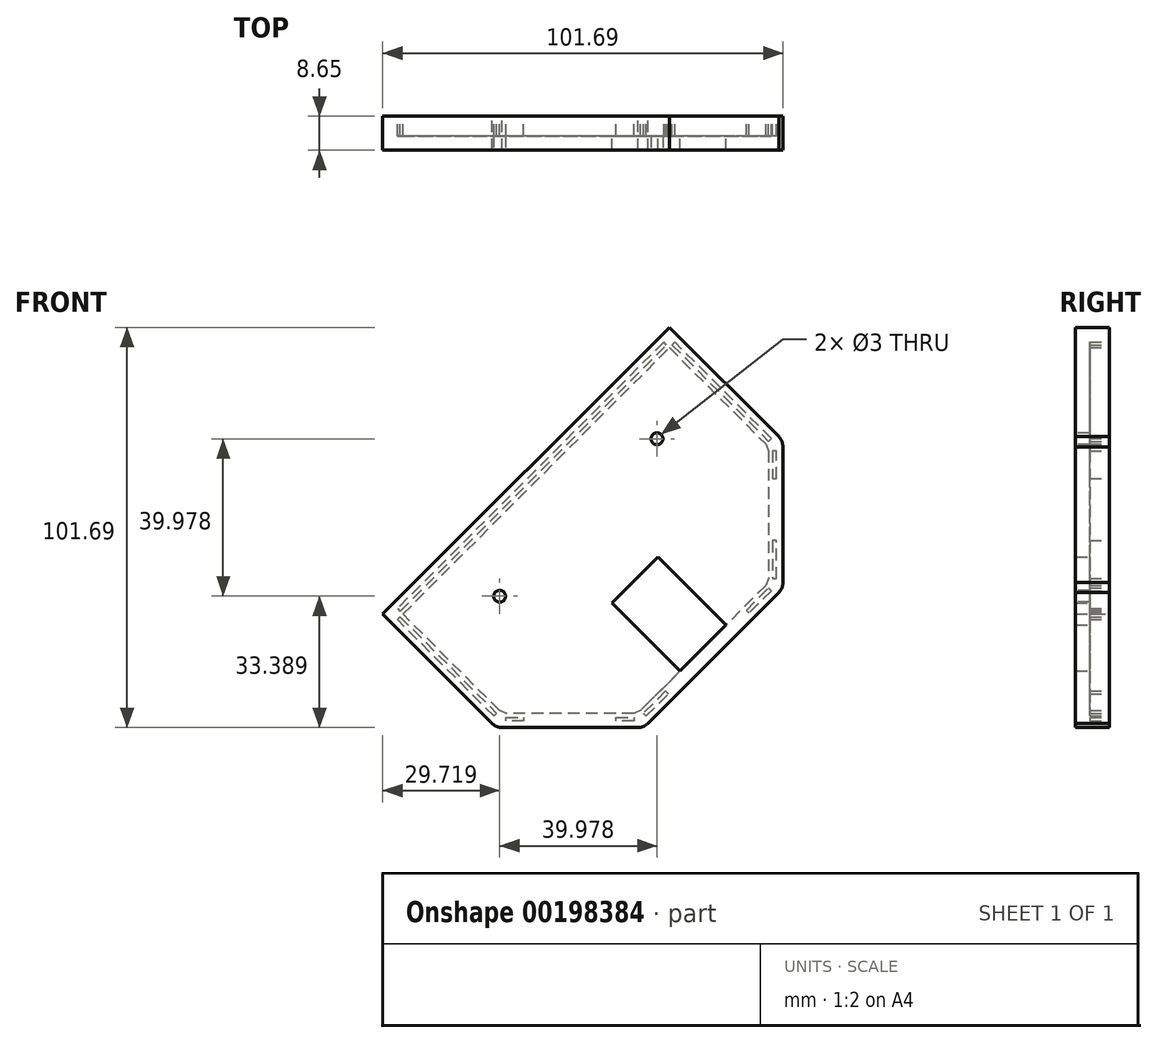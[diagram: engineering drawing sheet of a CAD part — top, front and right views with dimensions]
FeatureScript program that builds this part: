
annotation { "Feature Type Name" : "Feature", "Feature Type Description" : "" }
export const myFeature = defineFeature(function(context is Context, id is Id, definition is map)
    precondition{}
    {
        {
            var Q0;
            Q0=qCreatedBy(makeId("Front.planeOp"),FACE);
            var sketch = newSketch(context, id + "F0", { "sketchPlane" : qUnion([Q0])});
            skLineSegment(sketch, "E0", {"start": v(6.59, 67.44) * mm, "end": v(-66.27, -5.41) * mm});
            skLineSegment(sketch, "E1", {"start": v(-66.27, -5.41) * mm, "end": v(-38.5, -33.18) * mm});
            skFitSpline(sketch, "E2", {"points": [v(-38.5, -33.18) * mm, v(-37.32, -33.98) * mm, v(-35.92, -34.25) * mm], "startDerivative": vector(2.26, -1.84) * mm, "endDerivative": vector(2.9, -0.3) * mm});
            skLineSegment(sketch, "E3", {"start": v(-35.92, -34.25) * mm, "end": v(-1.44, -34.25) * mm});
            skFitSpline(sketch, "E4", {"points": [v(-1.44, -34.25) * mm, v(-0.05, -33.98) * mm, v(1.14, -33.18) * mm], "startDerivative": vector(2.9, 0.3) * mm, "endDerivative": vector(2.26, 1.84) * mm});
            skLineSegment(sketch, "E5", {"start": v(1.14, -33.18) * mm, "end": v(34.35, 0.03) * mm});
            skFitSpline(sketch, "E6", {"points": [v(35.42, 37.1) * mm, v(35.15, 38.49) * mm, v(34.35, 39.67) * mm], "startDerivative": vector(-0.3, 2.9) * mm, "endDerivative": vector(-1.84, 2.26) * mm});
            skLineSegment(sketch, "E7", {"start": v(34.35, 39.67) * mm, "end": v(6.59, 67.44) * mm});
            skLineSegment(sketch, "E8", {"start": v(6.59, 62.28) * mm, "end": v(31.07, 37.8) * mm});
            skLineSegment(sketch, "E9", {"start": v(31.07, 37.8) * mm, "end": v(31.77, 36.1) * mm});
            skLineSegment(sketch, "E10", {"start": v(31.77, 36.1) * mm, "end": v(31.77, 3.61) * mm});
            skLineSegment(sketch, "E11", {"start": v(31.77, 3.61) * mm, "end": v(31.07, 1.9) * mm});
            skLineSegment(sketch, "E12", {"start": v(31.07, 1.9) * mm, "end": v(25.42, -3.74) * mm});
            skLineSegment(sketch, "E13", {"start": v(25.42, -3.74) * mm, "end": v(-0.74, -29.9) * mm});
            skLineSegment(sketch, "E14", {"start": v(-0.74, -29.9) * mm, "end": v(-2.44, -30.6) * mm});
            skLineSegment(sketch, "E15", {"start": v(-2.44, -30.6) * mm, "end": v(-6.93, -30.6) * mm});
            skLineSegment(sketch, "E16", {"start": v(-6.93, -30.6) * mm, "end": v(-30.43, -30.6) * mm});
            skLineSegment(sketch, "E17", {"start": v(-30.43, -30.6) * mm, "end": v(-34.92, -30.6) * mm});
            skLineSegment(sketch, "E18", {"start": v(-34.92, -30.6) * mm, "end": v(-36.63, -29.9) * mm});
            skLineSegment(sketch, "E19", {"start": v(-36.63, -29.9) * mm, "end": v(-61.1, -5.41) * mm});
            skLineSegment(sketch, "E20", {"start": v(-61.1, -5.41) * mm, "end": v(6.59, 62.28) * mm});
            skLineSegment(sketch, "E21", {"start": v(32.48, 39.21) * mm, "end": v(8, 63.7) * mm});
            skLineSegment(sketch, "E22", {"start": v(8, 63.7) * mm, "end": v(7.3, 62.99) * mm});
            skLineSegment(sketch, "E23", {"start": v(7.3, 62.99) * mm, "end": v(31.77, 38.5) * mm});
            skLineSegment(sketch, "E24", {"start": v(31.77, 38.5) * mm, "end": v(32.48, 39.21) * mm});
            skLineSegment(sketch, "E25", {"start": v(5.17, 63.7) * mm, "end": v(-62.52, -4) * mm});
            skLineSegment(sketch, "E26", {"start": v(-62.52, -4) * mm, "end": v(-61.81, -4.7) * mm});
            skLineSegment(sketch, "E27", {"start": v(-61.81, -4.7) * mm, "end": v(5.88, 62.99) * mm});
            skLineSegment(sketch, "E28", {"start": v(5.88, 62.99) * mm, "end": v(5.17, 63.7) * mm});
            skLineSegment(sketch, "E29", {"start": v(33.77, 36.1) * mm, "end": v(32.77, 36.1) * mm});
            skLineSegment(sketch, "E30", {"start": v(32.77, 36.1) * mm, "end": v(32.77, 28.98) * mm});
            skLineSegment(sketch, "E31", {"start": v(32.77, 28.98) * mm, "end": v(33.77, 28.98) * mm});
            skLineSegment(sketch, "E32", {"start": v(33.77, 28.98) * mm, "end": v(33.77, 36.1) * mm});
            skLineSegment(sketch, "E33", {"start": v(-37.33, -30.6) * mm, "end": v(-38.04, -31.31) * mm});
            skLineSegment(sketch, "E34", {"start": v(-38.04, -31.31) * mm, "end": v(-62.52, -6.83) * mm});
            skLineSegment(sketch, "E35", {"start": v(-62.52, -6.83) * mm, "end": v(-61.81, -6.12) * mm});
            skLineSegment(sketch, "E36", {"start": v(-61.81, -6.12) * mm, "end": v(-37.33, -30.6) * mm});
            skLineSegment(sketch, "E37", {"start": v(-30.43, -32.6) * mm, "end": v(-34.92, -32.6) * mm});
            skLineSegment(sketch, "E38", {"start": v(-34.92, -32.6) * mm, "end": v(-34.92, -31.6) * mm});
            skLineSegment(sketch, "E39", {"start": v(-34.92, -31.6) * mm, "end": v(-30.43, -31.6) * mm});
            skLineSegment(sketch, "E40", {"start": v(-30.43, -31.6) * mm, "end": v(-30.43, -32.6) * mm});
            skLineSegment(sketch, "E41", {"start": v(-2.44, -32.6) * mm, "end": v(-6.93, -32.6) * mm});
            skLineSegment(sketch, "E42", {"start": v(-6.93, -32.6) * mm, "end": v(-6.93, -31.6) * mm});
            skLineSegment(sketch, "E43", {"start": v(-6.93, -31.6) * mm, "end": v(-2.44, -31.6) * mm});
            skLineSegment(sketch, "E44", {"start": v(-2.44, -31.6) * mm, "end": v(-2.44, -32.6) * mm});
            skLineSegment(sketch, "E45", {"start": v(6.33, -25.66) * mm, "end": v(5.62, -24.95) * mm});
            skLineSegment(sketch, "E46", {"start": v(5.62, -24.95) * mm, "end": v(-0.03, -30.6) * mm});
            skLineSegment(sketch, "E47", {"start": v(-0.03, -30.6) * mm, "end": v(0.68, -31.31) * mm});
            skLineSegment(sketch, "E48", {"start": v(0.68, -31.31) * mm, "end": v(6.33, -25.66) * mm});
            skLineSegment(sketch, "E49", {"start": v(26.83, -5.16) * mm, "end": v(26.13, -4.45) * mm});
            skLineSegment(sketch, "E50", {"start": v(26.13, -4.45) * mm, "end": v(31.77, 1.2) * mm});
            skLineSegment(sketch, "E51", {"start": v(31.77, 1.2) * mm, "end": v(32.48, 0.5) * mm});
            skLineSegment(sketch, "E52", {"start": v(32.48, 0.5) * mm, "end": v(26.83, -5.16) * mm});
            skLineSegment(sketch, "E53", {"start": v(33.77, 3.61) * mm, "end": v(33.77, 13.23) * mm});
            skLineSegment(sketch, "E54", {"start": v(33.77, 13.23) * mm, "end": v(32.77, 13.23) * mm});
            skLineSegment(sketch, "E55", {"start": v(32.77, 13.23) * mm, "end": v(32.77, 3.61) * mm});
            skLineSegment(sketch, "E56", {"start": v(32.77, 3.61) * mm, "end": v(33.77, 3.61) * mm});
            skLineSegment(sketch, "E57", {"start": v(17.75, -16.58) * mm, "end": v(-0.03, 1.2) * mm});
            skFitSpline(sketch, "E58", {"points": [v(34.35, 0.03) * mm, v(35.15, 1.22) * mm, v(35.42, 2.61) * mm], "startDerivative": vector(1.84, 2.26) * mm, "endDerivative": vector(0.3, 2.9) * mm});
            skLineSegment(sketch, "E59", {"start": v(35.42, 37.1) * mm, "end": v(35.42, 2.61) * mm});
            skSolve(sketch);
        }
        {
            var Q0;
            Q0=makeQuery(id+"F0.imprint","IMPRINT",FACE,{"disambiguationData":[TD([[makeQuery(id+"F0.imprint","IMPRINT",EDGE,{"derivedFrom":sQuery(id+"F0.wireOp",EDGE,"E29")}),1.0]])]});
            var Q1;
            Q1=makeQuery(id+"F0.imprint","IMPRINT",FACE,{"disambiguationData":[TD([[makeQuery(id+"F0.imprint","IMPRINT",EDGE,{"derivedFrom":sQuery(id+"F0.wireOp",EDGE,"E21")}),1.0]])]});
            var Q2;
            Q2=makeQuery(id+"F0.imprint","IMPRINT",FACE,{"disambiguationData":[TD([[makeQuery(id+"F0.imprint","IMPRINT",EDGE,{"derivedFrom":sQuery(id+"F0.wireOp",EDGE,"E53")}),1.0]])]});
            var Q3;
            Q3=makeQuery(id+"F0.imprint","IMPRINT",FACE,{"disambiguationData":[TD([[makeQuery(id+"F0.imprint","IMPRINT",EDGE,{"derivedFrom":sQuery(id+"F0.wireOp",EDGE,"E49")}),-1.0]])]});
            var Q4;
            Q4=makeQuery(id+"F0.imprint","IMPRINT",FACE,{"disambiguationData":[TD([[makeQuery(id+"F0.imprint","IMPRINT",EDGE,{"derivedFrom":sQuery(id+"F0.wireOp",EDGE,"E45")}),1.0]])]});
            var Q5;
            Q5=makeQuery(id+"F0.imprint","IMPRINT",FACE,{"disambiguationData":[TD([[makeQuery(id+"F0.imprint","IMPRINT",EDGE,{"derivedFrom":sQuery(id+"F0.wireOp",EDGE,"E41")}),-1.0]])]});
            var Q6;
            Q6=makeQuery(id+"F0.imprint","IMPRINT",FACE,{"disambiguationData":[TD([[makeQuery(id+"F0.imprint","IMPRINT",EDGE,{"derivedFrom":sQuery(id+"F0.wireOp",EDGE,"E37")}),-1.0]])]});
            var Q7;
            Q7=makeQuery(id+"F0.imprint","IMPRINT",FACE,{"disambiguationData":[TD([[makeQuery(id+"F0.imprint","IMPRINT",EDGE,{"derivedFrom":sQuery(id+"F0.wireOp",EDGE,"E33")}),-1.0]])]});
            var Q8;
            Q8=makeQuery(id+"F0.imprint","IMPRINT",FACE,{"disambiguationData":[TD([[makeQuery(id+"F0.imprint","IMPRINT",EDGE,{"derivedFrom":sQuery(id+"F0.wireOp",EDGE,"E25")}),1.0]])]});
            var Q9;
            Q9=makeQuery(id+"F0.imprint","IMPRINT",FACE,{"disambiguationData":[TD([[makeQuery(id+"F0.imprint","IMPRINT",EDGE,{"derivedFrom":sQuery(id+"F0.wireOp",EDGE,"E0")}),1.0]])]});
            var Q10;
            Q10=makeQuery(id+"F0.imprint","IMPRINT",FACE,{"disambiguationData":[TD([[makeQuery(id+"F0.imprint","IMPRINT",EDGE,{"derivedFrom":sQuery(id+"F0.wireOp",EDGE,"E8")}),-1.0]])]});
            extrude(context, id + "F1", {"entities" : qUnion([Q0, Q1, Q2, Q3, Q4, Q5, Q6, Q7, Q8, Q9, Q10]), "depth" : 8.65 * mm});
        }
        {
            var Q0;
            Q0=makeQuery(id+"F0.imprint","IMPRINT",FACE,{"disambiguationData":[TD([[makeQuery(id+"F0.imprint","IMPRINT",EDGE,{"derivedFrom":sQuery(id+"F0.wireOp",EDGE,"E8")}),-1.0]])]});
            extrude(context, id + "F2", {"entities" : qUnion([Q0]), "operationType" : NewBodyOperationType.REMOVE, "depth" : 5 * mm});
        }
        {
            var Q0;
            Q0=makeQuery(id+"F0.imprint","IMPRINT",FACE,{"disambiguationData":[TD([[makeQuery(id+"F0.imprint","IMPRINT",EDGE,{"derivedFrom":sQuery(id+"F0.wireOp",EDGE,"E21")}),1.0]])]});
            var Q1;
            Q1=makeQuery(id+"F0.imprint","IMPRINT",FACE,{"disambiguationData":[TD([[makeQuery(id+"F0.imprint","IMPRINT",EDGE,{"derivedFrom":sQuery(id+"F0.wireOp",EDGE,"E25")}),1.0]])]});
            var Q2;
            Q2=makeQuery(id+"F0.imprint","IMPRINT",FACE,{"disambiguationData":[TD([[makeQuery(id+"F0.imprint","IMPRINT",EDGE,{"derivedFrom":sQuery(id+"F0.wireOp",EDGE,"E33")}),-1.0]])]});
            var Q3;
            Q3=makeQuery(id+"F0.imprint","IMPRINT",FACE,{"disambiguationData":[TD([[makeQuery(id+"F0.imprint","IMPRINT",EDGE,{"derivedFrom":sQuery(id+"F0.wireOp",EDGE,"E37")}),-1.0]])]});
            var Q4;
            Q4=makeQuery(id+"F0.imprint","IMPRINT",FACE,{"disambiguationData":[TD([[makeQuery(id+"F0.imprint","IMPRINT",EDGE,{"derivedFrom":sQuery(id+"F0.wireOp",EDGE,"E41")}),-1.0]])]});
            var Q5;
            Q5=makeQuery(id+"F0.imprint","IMPRINT",FACE,{"disambiguationData":[TD([[makeQuery(id+"F0.imprint","IMPRINT",EDGE,{"derivedFrom":sQuery(id+"F0.wireOp",EDGE,"E45")}),1.0]])]});
            var Q6;
            Q6=makeQuery(id+"F0.imprint","IMPRINT",FACE,{"disambiguationData":[TD([[makeQuery(id+"F0.imprint","IMPRINT",EDGE,{"derivedFrom":sQuery(id+"F0.wireOp",EDGE,"E49")}),-1.0]])]});
            var Q7;
            Q7=makeQuery(id+"F0.imprint","IMPRINT",FACE,{"disambiguationData":[TD([[makeQuery(id+"F0.imprint","IMPRINT",EDGE,{"derivedFrom":sQuery(id+"F0.wireOp",EDGE,"E53")}),1.0]])]});
            var Q8;
            Q8=makeQuery(id+"F0.imprint","IMPRINT",FACE,{"disambiguationData":[TD([[makeQuery(id+"F0.imprint","IMPRINT",EDGE,{"derivedFrom":sQuery(id+"F0.wireOp",EDGE,"E29")}),1.0]])]});
            extrude(context, id + "F3", {"entities" : qUnion([Q0, Q1, Q2, Q3, Q4, Q5, Q6, Q7, Q8]), "operationType" : NewBodyOperationType.REMOVE, "depth" : 5 * mm});
        }
        {
            var Q0;
            Q0=makeQuery(id+"F2.boolean.opBoolean","COPY",FACE,{"derivedFrom":makeQuery(id+"F2.opExtrude","CAP_FACE",FACE,{"disambiguationData":[OSD([sQuery(id+"F0.wireOp",EDGE,"E8"),sQuery(id+"F0.wireOp",EDGE,"E9"),sQuery(id+"F0.wireOp",EDGE,"E10"),sQuery(id+"F0.wireOp",EDGE,"E11"),sQuery(id+"F0.wireOp",EDGE,"E12"),sQuery(id+"F0.wireOp",EDGE,"E13"),sQuery(id+"F0.wireOp",EDGE,"E14"),sQuery(id+"F0.wireOp",EDGE,"E15"),sQuery(id+"F0.wireOp",EDGE,"E16"),sQuery(id+"F0.wireOp",EDGE,"E17"),sQuery(id+"F0.wireOp",EDGE,"E18"),sQuery(id+"F0.wireOp",EDGE,"E19"),sQuery(id+"F0.wireOp",EDGE,"E20"),sQuery(id+"F0.wireOp",EDGE,"a02296cc-774d-4582-bdce-437602296666"),sQuery(id+"F0.wireOp",EDGE,"6a258dab-7cfd-4e8a-b6b1-9d2fc9da9d98")])],"isStart":false})});
            var sketch = newSketch(context, id + "F4", { "sketchPlane" : qUnion([Q0])});
            skLineSegment(sketch, "E60", {"start": v(-20.96, -8.2) * mm, "end": v(-3.64, 9.13) * mm});
            skLineSegment(sketch, "E61", {"start": v(-3.64, 9.13) * mm, "end": v(8.03, -2.54) * mm});
            skLineSegment(sketch, "E62", {"start": v(8.03, -2.54) * mm, "end": v(-9.3, -19.86) * mm});
            skLineSegment(sketch, "E63", {"start": v(-9.3, -19.86) * mm, "end": v(-20.96, -8.2) * mm});
            skSolve(sketch);
        }
        {
            var Q0;
            Q0=makeQuery(id+"F4.imprint","IMPRINT",FACE,{"disambiguationData":[TD([[makeQuery(id+"F4.imprint","IMPRINT",EDGE,{"derivedFrom":sQuery(id+"F4.wireOp",EDGE,"E60")}),-1.0]])]});
            var Q1;
            Q1=makeQuery(id+"F1.opExtrude","CAP_FACE",FACE,{"disambiguationData":[OSD([sQuery(id+"F0.wireOp",EDGE,"E0"),sQuery(id+"F0.wireOp",EDGE,"E1"),sQuery(id+"F0.wireOp",EDGE,"E2"),sQuery(id+"F0.wireOp",EDGE,"E3"),sQuery(id+"F0.wireOp",EDGE,"E4"),sQuery(id+"F0.wireOp",EDGE,"E5"),sQuery(id+"F0.wireOp",EDGE,"E6"),sQuery(id+"F0.wireOp",EDGE,"E7"),sQuery(id+"F0.wireOp",EDGE,"a02296cc-774d-4582-bdce-437602296666"),sQuery(id+"F0.wireOp",EDGE,"6a258dab-7cfd-4e8a-b6b1-9d2fc9da9d98"),sQuery(id+"F0.wireOp",EDGE,"E58"),sQuery(id+"F0.wireOp",EDGE,"E59")])],"isStart":false});
            extrude(context, id + "F5", {"entities" : qUnion([Q0]), "operationType" : NewBodyOperationType.REMOVE, "endBound" : BoundingType.UP_TO_SURFACE, "oppositeDirection" : true, "endBoundEntityFace" : qUnion([Q1]), "depth" : 25.4 * mm});
        }
        {
            var Q0;
            Q0=makeQuery(id+"F1.opExtrude","CAP_FACE",FACE,{"disambiguationData":[OSD([sQuery(id+"F0.wireOp",EDGE,"E0"),sQuery(id+"F0.wireOp",EDGE,"E1"),sQuery(id+"F0.wireOp",EDGE,"E2"),sQuery(id+"F0.wireOp",EDGE,"E3"),sQuery(id+"F0.wireOp",EDGE,"E4"),sQuery(id+"F0.wireOp",EDGE,"E5"),sQuery(id+"F0.wireOp",EDGE,"E6"),sQuery(id+"F0.wireOp",EDGE,"E7"),sQuery(id+"F0.wireOp",EDGE,"a02296cc-774d-4582-bdce-437602296666"),sQuery(id+"F0.wireOp",EDGE,"6a258dab-7cfd-4e8a-b6b1-9d2fc9da9d98"),sQuery(id+"F0.wireOp",EDGE,"E58"),sQuery(id+"F0.wireOp",EDGE,"E59")])],"isStart":false});
            var sketch = newSketch(context, id + "F6", { "sketchPlane" : qUnion([Q0])});
            skCircle(sketch, "E64", {"center": v(3.43, 39.12) * mm, "radius": 1.5 * mm});
            skCircle(sketch, "E65", {"center": v(-36.55, -0.86) * mm, "radius": 1.5 * mm});
            skSolve(sketch);
        }
        {
            var Q0;
            Q0=makeQuery(id+"F6.imprint","IMPRINT",FACE,{"disambiguationData":[TD([[makeQuery(id+"F6.imprint","IMPRINT",EDGE,{"derivedFrom":sQuery(id+"F6.wireOp",EDGE,"E64")}),1.0]])]});
            var Q1;
            Q1=makeQuery(id+"F6.imprint","IMPRINT",FACE,{"disambiguationData":[TD([[makeQuery(id+"F6.imprint","IMPRINT",EDGE,{"derivedFrom":sQuery(id+"F6.wireOp",EDGE,"E65")}),1.0]])]});
            var Q2;
            Q2=makeQuery(id+"F2.boolean.opBoolean","COPY",FACE,{"derivedFrom":makeQuery(id+"F2.opExtrude","CAP_FACE",FACE,{"disambiguationData":[OSD([sQuery(id+"F0.wireOp",EDGE,"E8"),sQuery(id+"F0.wireOp",EDGE,"E9"),sQuery(id+"F0.wireOp",EDGE,"E10"),sQuery(id+"F0.wireOp",EDGE,"E11"),sQuery(id+"F0.wireOp",EDGE,"E12"),sQuery(id+"F0.wireOp",EDGE,"E13"),sQuery(id+"F0.wireOp",EDGE,"E14"),sQuery(id+"F0.wireOp",EDGE,"E15"),sQuery(id+"F0.wireOp",EDGE,"E16"),sQuery(id+"F0.wireOp",EDGE,"E17"),sQuery(id+"F0.wireOp",EDGE,"E18"),sQuery(id+"F0.wireOp",EDGE,"E19"),sQuery(id+"F0.wireOp",EDGE,"E20"),sQuery(id+"F0.wireOp",EDGE,"a02296cc-774d-4582-bdce-437602296666"),sQuery(id+"F0.wireOp",EDGE,"6a258dab-7cfd-4e8a-b6b1-9d2fc9da9d98")])],"isStart":false})});
            extrude(context, id + "F7", {"entities" : qUnion([Q0, Q1]), "operationType" : NewBodyOperationType.REMOVE, "endBound" : BoundingType.UP_TO_SURFACE, "oppositeDirection" : true, "endBoundEntityFace" : qUnion([Q2]), "depth" : 25.4 * mm});
        }
    });
